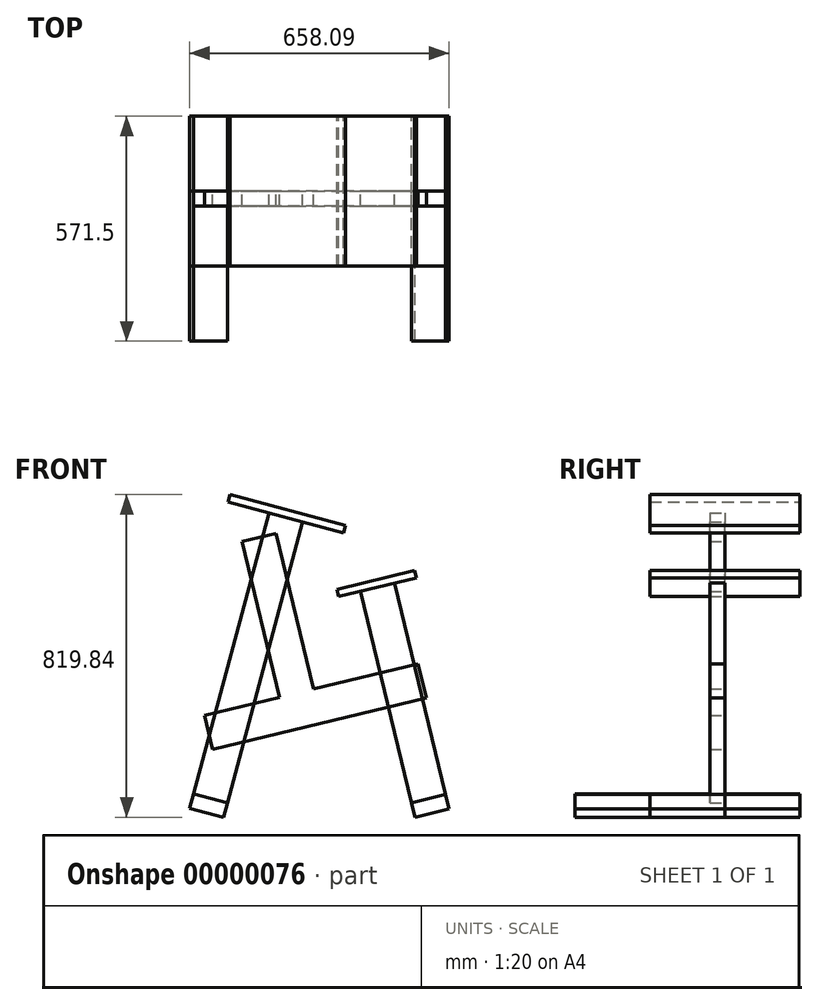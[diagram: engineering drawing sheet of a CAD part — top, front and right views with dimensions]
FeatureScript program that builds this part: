
annotation { "Feature Type Name" : "Feature", "Feature Type Description" : "" }
export const myFeature = defineFeature(function(context is Context, id is Id, definition is map)
    precondition{}
    {
        {
            var Q0;
            Q0=qCreatedBy(makeId("Front.planeOp"),FACE);
            var sketch = newSketch(context, id + "F0", { "sketchPlane" : qUnion([Q0])});
            skLineSegment(sketch, "E0", {"start": v(-142.28, 819.84) * mm, "end": v(-147.2, 801.44) * mm});
            skLineSegment(sketch, "E1", {"start": v(-147.2, 801.44) * mm, "end": v(147.2, 722.56) * mm});
            skLineSegment(sketch, "E2", {"start": v(147.2, 722.56) * mm, "end": v(152.14, 740.96) * mm});
            skLineSegment(sketch, "E3", {"start": v(152.14, 740.96) * mm, "end": v(-142.28, 819.84) * mm});
            skLineSegment(sketch, "E4", {"start": v(0, 762) * mm, "end": v(0, 0) * mm, "construction": true});
            skLineSegment(sketch, "E5", {"start": v(129.53, 579.25) * mm, "end": v(327.1, 626.76) * mm});
            skLineSegment(sketch, "E6", {"start": v(327.1, 626.76) * mm, "end": v(331.55, 608.24) * mm});
            skLineSegment(sketch, "E7", {"start": v(331.55, 608.24) * mm, "end": v(133.98, 560.73) * mm});
            skLineSegment(sketch, "E8", {"start": v(133.98, 560.73) * mm, "end": v(129.53, 579.25) * mm});
            skLineSegment(sketch, "E9", {"start": v(-42.94, 773.5) * mm, "end": v(-234.17, 59.81) * mm});
            skLineSegment(sketch, "E10", {"start": v(-234.17, 59.81) * mm, "end": v(-148.3, 36.8) * mm});
            skLineSegment(sketch, "E11", {"start": v(-148.3, 36.8) * mm, "end": v(42.94, 750.5) * mm});
            skLineSegment(sketch, "E12", {"start": v(-234.17, 59.81) * mm, "end": v(-244.03, 23) * mm});
            skLineSegment(sketch, "E13", {"start": v(-244.03, 23) * mm, "end": v(-158.16, 0) * mm});
            skLineSegment(sketch, "E14", {"start": v(-158.16, 0) * mm, "end": v(-148.3, 36.8) * mm});
            skLineSegment(sketch, "E15", {"start": v(189.55, 574.09) * mm, "end": v(318.71, 37.04) * mm});
            skLineSegment(sketch, "E16", {"start": v(318.71, 37.04) * mm, "end": v(405.15, 57.83) * mm});
            skLineSegment(sketch, "E17", {"start": v(405.15, 57.83) * mm, "end": v(275.98, 594.88) * mm});
            skLineSegment(sketch, "E18", {"start": v(318.71, 37.04) * mm, "end": v(327.62, 0) * mm});
            skLineSegment(sketch, "E19", {"start": v(327.62, 0) * mm, "end": v(414.06, 20.79) * mm});
            skLineSegment(sketch, "E20", {"start": v(414.06, 20.79) * mm, "end": v(405.15, 57.83) * mm});
            skLineSegment(sketch, "E21", {"start": v(0, 762) * mm, "end": v(-191.23, 48.3) * mm, "construction": true});
            skLineSegment(sketch, "E22", {"start": v(232.76, 584.48) * mm, "end": v(361.93, 47.44) * mm, "construction": true});
            skLineSegment(sketch, "E23", {"start": v(-142.82, 228.98) * mm, "end": v(293.05, 333.8) * mm, "construction": true});
            skLineSegment(sketch, "E24", {"start": v(37.33, 272.3) * mm, "end": v(-42.4, 603.8) * mm, "construction": true});
            skCircle(sketch, "E25", {"center": v(44.13, 848.78) * mm, "radius": 76.2 * mm, "construction": true});
            skLineSegment(sketch, "E26", {"start": v(44.13, 848.78) * mm, "end": v(398.68, 709.3) * mm, "construction": true});
            skLineSegment(sketch, "E27", {"start": v(398.68, 709.3) * mm, "end": v(28.24, 620.2) * mm, "construction": true});
            skLineSegment(sketch, "E28", {"start": v(213.46, 664.75) * mm, "end": v(228.3, 603) * mm, "construction": true});
            skSolve(sketch);
        }
        {
            var Q0;
            Q0=qCreatedBy(makeId("Front.planeOp"),FACE);
            var sketch = newSketch(context, id + "F1", { "sketchPlane" : qUnion([Q0])});
            skLineSegment(sketch, "E29", {"start": v(-206.93, 259.28) * mm, "end": v(336.37, 389.95) * mm});
            skLineSegment(sketch, "E30", {"start": v(336.37, 389.95) * mm, "end": v(357.16, 303.51) * mm});
            skLineSegment(sketch, "E31", {"start": v(357.16, 303.51) * mm, "end": v(-186.14, 172.84) * mm});
            skLineSegment(sketch, "E32", {"start": v(-186.14, 172.84) * mm, "end": v(-206.93, 259.28) * mm});
            skLineSegment(sketch, "E33", {"start": v(-111.31, 700.26) * mm, "end": v(-16.28, 305.13) * mm});
            skLineSegment(sketch, "E34", {"start": v(-111.31, 700.26) * mm, "end": v(-24.88, 721.05) * mm});
            skLineSegment(sketch, "E35", {"start": v(-24.88, 721.05) * mm, "end": v(70.16, 325.92) * mm});
            skLineSegment(sketch, "E36", {"start": v(-206.93, 259.28) * mm, "end": v(357.16, 303.51) * mm, "construction": true});
            skLineSegment(sketch, "E37", {"start": v(-111.31, 700.26) * mm, "end": v(70.16, 325.92) * mm, "construction": true});
            skPoint(sketch, "E38", {"position": v(-20.58, 513.1) * mm});
            skPoint(sketch, "E39", {"position": v(75.12, 281.4) * mm});
            skSolve(sketch);
        }
        {
            var Q0;
            {var subQ4=sQuery(id+"F0.wireOp",EDGE,"E0");Q0=makeQuery(id+"F0.imprint","IMPRINT",FACE,{"disambiguationData":[TD([[makeQuery(id+"F0.imprint","IMPRINT",EDGE,{"derivedFrom":subQ4}),1.0]])]});}
            var Q1;
            Q1=makeQuery(id+"F0.imprint","IMPRINT",FACE,{"disambiguationData":[TD([[makeQuery(id+"F0.imprint","IMPRINT",EDGE,{"derivedFrom":sQuery(id+"F0.wireOp",EDGE,"E5")}),-1.0]])]});
            var Q2;
            Q2=makeQuery(id+"F0.imprint","IMPRINT",FACE,{"disambiguationData":[TD([[makeQuery(id+"F0.imprint","IMPRINT",EDGE,{"derivedFrom":sQuery(id+"F0.wireOp",EDGE,"E10")}),-1.0]])]});
            var Q3;
            Q3=makeQuery(id+"F0.imprint","IMPRINT",FACE,{"disambiguationData":[TD([[makeQuery(id+"F0.imprint","IMPRINT",EDGE,{"derivedFrom":sQuery(id+"F0.wireOp",EDGE,"E16")}),-1.0]])]});
            extrude(context, id + "F2", {"entities" : qUnion([Q0, Q1, Q2, Q3]), "depth" : 381 * mm, "symmetric" : true});
        }
        {
            var Q0;
            {var subQ1=sQuery(id+"F0.wireOp",EDGE,"E9");Q0=makeQuery(id+"F0.imprint","IMPRINT",FACE,{"disambiguationData":[TD([[makeQuery(id+"F0.imprint","IMPRINT",EDGE,{"derivedFrom":subQ1}),1.0]])]});}
            var Q1;
            {var subQ1=sQuery(id+"F0.wireOp",EDGE,"E15");Q1=makeQuery(id+"F0.imprint","IMPRINT",FACE,{"disambiguationData":[TD([[makeQuery(id+"F0.imprint","IMPRINT",EDGE,{"derivedFrom":subQ1}),1.0]])]});}
            extrude(context, id + "F3", {"entities" : qUnion([Q0, Q1]), "depth" : 38.1 * mm});
        }
        {
            var Q0;
            {var subQ1=sQuery(id+"F1.wireOp",EDGE,"E33");Q0=makeQuery(id+"F1.imprint","IMPRINT",FACE,{"disambiguationData":[TD([[makeQuery(id+"F1.imprint","IMPRINT",EDGE,{"derivedFrom":subQ1}),1.0]])]});}
            var Q1;
            {var subQ1=sQuery(id+"F1.wireOp",EDGE,"E30");Q1=makeQuery(id+"F1.imprint","IMPRINT",FACE,{"disambiguationData":[TD([[makeQuery(id+"F1.imprint","IMPRINT",EDGE,{"derivedFrom":subQ1}),-1.0]])]});}
            extrude(context, id + "F4", {"entities" : qUnion([Q0, Q1]), "depth" : 38.1 * mm});
        }
        {
            var Q0;
            Q0=makeQuery(id+"F0.imprint","IMPRINT",FACE,{"disambiguationData":[TD([[makeQuery(id+"F0.imprint","IMPRINT",EDGE,{"derivedFrom":sQuery(id+"F0.wireOp",EDGE,"E10")}),-1.0]])]});
            var Q1;
            Q1=makeQuery(id+"F0.imprint","IMPRINT",FACE,{"disambiguationData":[TD([[makeQuery(id+"F0.imprint","IMPRINT",EDGE,{"derivedFrom":sQuery(id+"F0.wireOp",EDGE,"E16")}),-1.0]])]});
            extrude(context, id + "F5", {"entities" : qUnion([Q0, Q1]), "depth" : 381 * mm});
        }
    });
